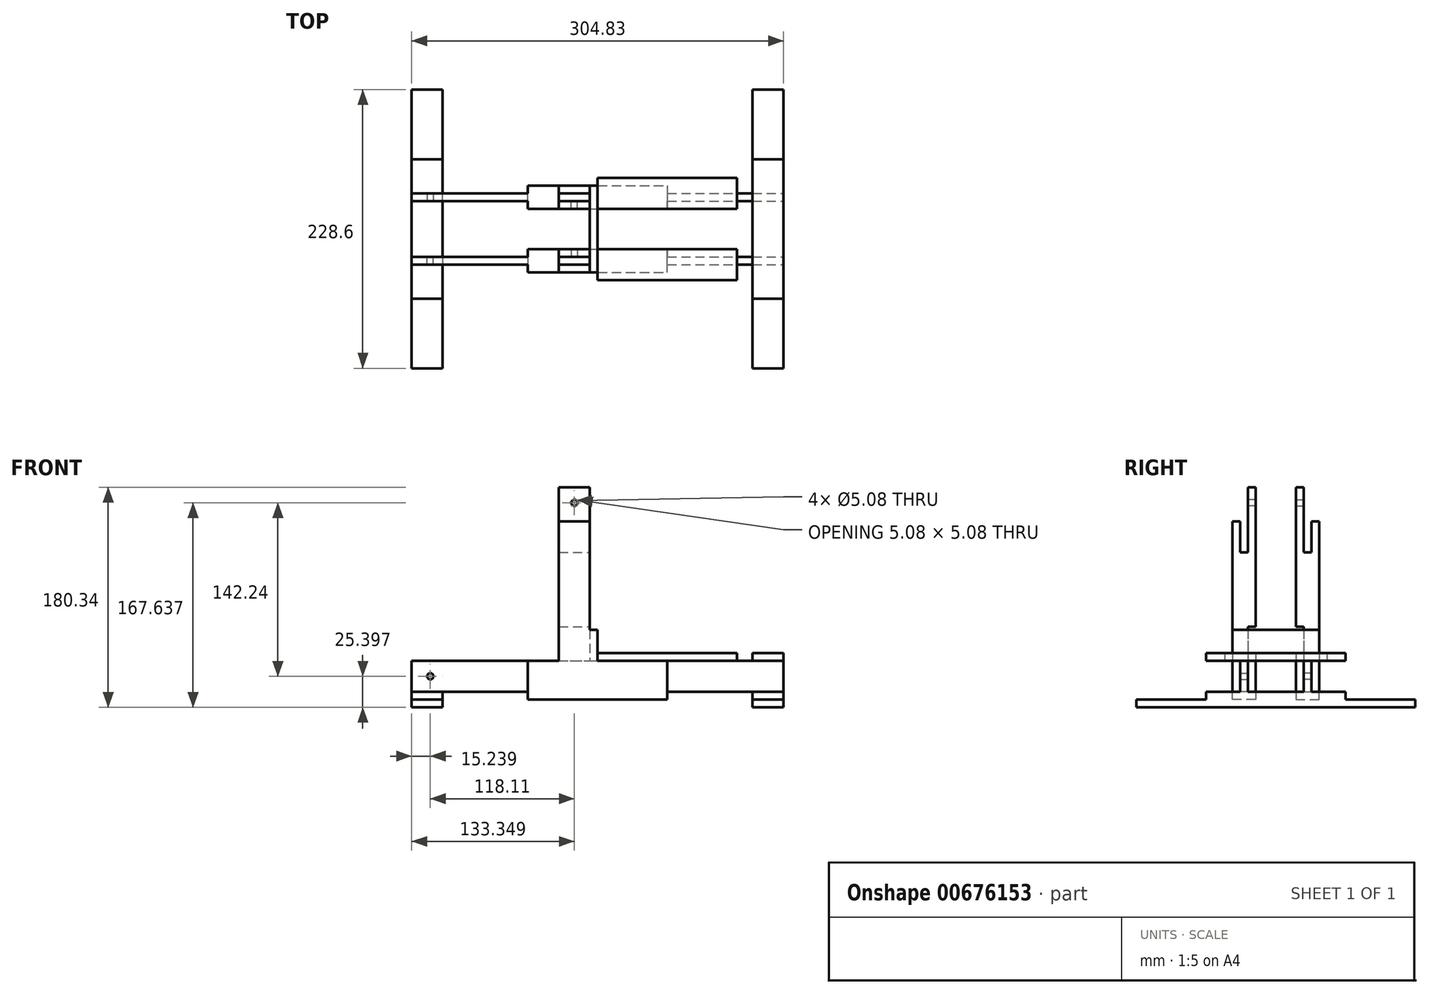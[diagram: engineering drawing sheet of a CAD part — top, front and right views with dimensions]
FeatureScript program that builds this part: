
annotation { "Feature Type Name" : "Feature", "Feature Type Description" : "" }
export const myFeature = defineFeature(function(context is Context, id is Id, definition is map)
    precondition{}
    {
        {
            var Q0;
            Q0=qCreatedBy(makeId("Front.planeOp"),FACE);
            var sketch = newSketch(context, id + "F0", { "sketchPlane" : qUnion([Q0])});
            skLineSegment(sketch, "E0.bottom", {"start": v(-142.94, -2.42) * mm, "end": v(161.86, -2.42) * mm});
            skLineSegment(sketch, "E0.top", {"start": v(-142.94, -27.82) * mm, "end": v(161.86, -27.82) * mm});
            skLineSegment(sketch, "E0.left", {"start": v(-142.94, -2.42) * mm, "end": v(-142.94, -27.82) * mm});
            skLineSegment(sketch, "E0.right", {"start": v(161.86, -2.42) * mm, "end": v(161.86, -27.82) * mm});
            skSolve(sketch);
        }
        {
            var Q0;
            Q0 = qSketchRegion(id + "F0", true);
            extrude(context, id + "F1", {"entities" : qUnion([Q0]), "depth" : 6.35 * mm, "offsetDistance" : 25.4 * mm});
        }
        {
            var Q0;
            Q0=makeQuery(id+"F1.opExtrude","CAP_FACE",FACE,{"disambiguationData":[OSD([sQuery(id+"F0.wireOp",EDGE,"E0.bottom"),sQuery(id+"F0.wireOp",EDGE,"E0.top"),sQuery(id+"F0.wireOp",EDGE,"E0.left"),sQuery(id+"F0.wireOp",EDGE,"E0.right")])],"isStart":false});
            var sketch = newSketch(context, id + "F2", { "sketchPlane" : qUnion([Q0])});
            skLineSegment(sketch, "E1.bottom", {"start": v(-47.7, -2.42) * mm, "end": v(66.6, -2.42) * mm});
            skLineSegment(sketch, "E1.top", {"start": v(-47.7, -27.82) * mm, "end": v(66.6, -27.82) * mm});
            skLineSegment(sketch, "E1.left", {"start": v(-47.7, -2.42) * mm, "end": v(-47.7, -27.82) * mm});
            skLineSegment(sketch, "E1.right", {"start": v(66.6, -2.42) * mm, "end": v(66.6, -27.82) * mm});
            skSolve(sketch);
        }
        {
            var Q0;
            Q0 = qSketchRegion(id + "F2", true);
            extrude(context, id + "F3", {"entities" : qUnion([Q0]), "operationType" : NewBodyOperationType.ADD, "depth" : 6.35 * mm, "offsetDistance" : 25.4 * mm});
        }
        {
            var Q0;
            Q0=makeQuery(id+"F1.opExtrude","CAP_FACE",FACE,{"disambiguationData":[OSD([sQuery(id+"F0.wireOp",EDGE,"E0.bottom"),sQuery(id+"F0.wireOp",EDGE,"E0.top"),sQuery(id+"F0.wireOp",EDGE,"E0.left"),sQuery(id+"F0.wireOp",EDGE,"E0.right")])],"isStart":true});
            var sketch = newSketch(context, id + "F4", { "sketchPlane" : qUnion([Q0])});
            skLineSegment(sketch, "E2.bottom", {"start": v(47.7, -27.82) * mm, "end": v(-66.6, -27.82) * mm});
            skLineSegment(sketch, "E2.top", {"start": v(47.7, -2.42) * mm, "end": v(-66.6, -2.42) * mm});
            skLineSegment(sketch, "E2.left", {"start": v(47.7, -27.82) * mm, "end": v(47.7, -2.42) * mm});
            skLineSegment(sketch, "E2.right", {"start": v(-66.6, -27.82) * mm, "end": v(-66.6, -2.42) * mm});
            skSolve(sketch);
        }
        {
            var Q0;
            Q0 = qSketchRegion(id + "F4", true);
            extrude(context, id + "F5", {"entities" : qUnion([Q0]), "operationType" : NewBodyOperationType.ADD, "depth" : 6.35 * mm, "offsetDistance" : 25.4 * mm});
        }
        {
            var Q0;
            {var subQ0=sQuery(id+"F0.wireOp",EDGE,"E0.left");var subQ1=sQuery(id+"F0.wireOp",EDGE,"E0.top");var subQ2=sQuery(id+"F0.wireOp",EDGE,"E0.bottom");Q0=makeQuery(id+"F3.boolean.opBoolean","SPLIT",FACE,{"disambiguationData":[TD([makeQuery(id+"F1.opExtrude","SWEPT_FACE",FACE,{"disambiguationData":[OSD([subQ0])]})])],"derivedFrom":makeQuery(id+"F1.opExtrude","CAP_FACE",FACE,{"disambiguationData":[OSD([subQ2,subQ1,subQ0,sQuery(id+"F0.wireOp",EDGE,"E0.right")])],"isStart":false})});}
            var sketch = newSketch(context, id + "F6", { "sketchPlane" : qUnion([Q0])});
            skCircle(sketch, "E3", {"center": v(-127.7, -15.12) * mm, "radius": 2.54 * mm});
            skPoint(sketch, "E3.centerSnap0", {"position": v(-142.94, -15.12) * mm});
            skSolve(sketch);
        }
        {
            var Q0;
            Q0=sQuery(id+"F6.wireOp",VERTEX,"E3.center");
            var Q1;
            Q1=makeQuery(id+"F1.opExtrude","SWEPT_BODY",BODY,{"disambiguationData":[OSD([sQuery(id+"F0.wireOp",EDGE,"E0.bottom"),sQuery(id+"F0.wireOp",EDGE,"E0.top"),sQuery(id+"F0.wireOp",EDGE,"E0.left"),sQuery(id+"F0.wireOp",EDGE,"E0.right")])]});
            hole(context, id + "F7", {"style" : HoleStyle.SIMPLE, "endStyle" : HoleEndStyle.THROUGH, "holeDiameter" : 5.08 * mm, "majorDiameter" : 6.35 * mm, "isTappedThrough" : true, "tappedDepth" : 12.7 * mm, "tapClearance" : 3, "locations" : qUnion([Q0]), "scope" : qUnion([Q1])});
        }
        {
            var Q0;
            Q0=makeQuery(id+"F5.boolean.opBoolean","MERGE",FACE,{"derivedFrom":[makeQuery(id+"F3.boolean.opBoolean","MERGE",FACE,{"derivedFrom":[makeQuery(id+"F1.opExtrude","SWEPT_FACE",FACE,{"disambiguationData":[OSD([sQuery(id+"F0.wireOp",EDGE,"E0.top")])]}),makeQuery(id+"F3.opExtrude","SWEPT_FACE",FACE,{"disambiguationData":[OSD([sQuery(id+"F2.wireOp",EDGE,"E1.top")])]})]}),makeQuery(id+"F5.opExtrude","SWEPT_FACE",FACE,{"disambiguationData":[OSD([sQuery(id+"F4.wireOp",EDGE,"E2.bottom")])]})]});
            var sketch = newSketch(context, id + "F8", { "sketchPlane" : qUnion([Q0])});
            skLineSegment(sketch, "E4.bottom", {"start": v(-47.7, 12.7) * mm, "end": v(66.6, 12.7) * mm});
            skLineSegment(sketch, "E4.top", {"start": v(-47.7, -6.35) * mm, "end": v(66.6, -6.35) * mm});
            skLineSegment(sketch, "E4.left", {"start": v(-47.7, 12.7) * mm, "end": v(-47.7, -6.35) * mm});
            skLineSegment(sketch, "E4.right", {"start": v(66.6, 12.7) * mm, "end": v(66.6, -6.35) * mm});
            skSolve(sketch);
        }
        {
            var Q0;
            Q0 = qSketchRegion(id + "F8", true);
            extrude(context, id + "F9", {"entities" : qUnion([Q0]), "operationType" : NewBodyOperationType.ADD, "depth" : 6.35 * mm, "offsetDistance" : 25.4 * mm});
        }
        {
            var Q0;
            {var subQ0=sQuery(id+"F0.wireOp",EDGE,"E0.left");var subQ2=sQuery(id+"F0.wireOp",EDGE,"E0.top");Q0=makeQuery(id+"F9.boolean.opBoolean","SPLIT",FACE,{"disambiguationData":[TD([makeQuery(id+"F1.opExtrude","SWEPT_FACE",FACE,{"disambiguationData":[OSD([subQ0])]})])],"derivedFrom":makeQuery(id+"F5.boolean.opBoolean","MERGE",FACE,{"derivedFrom":[makeQuery(id+"F3.boolean.opBoolean","MERGE",FACE,{"derivedFrom":[makeQuery(id+"F1.opExtrude","SWEPT_FACE",FACE,{"disambiguationData":[OSD([subQ2])]}),makeQuery(id+"F3.opExtrude","SWEPT_FACE",FACE,{"disambiguationData":[OSD([sQuery(id+"F2.wireOp",EDGE,"E1.top")])]})]}),makeQuery(id+"F5.opExtrude","SWEPT_FACE",FACE,{"disambiguationData":[OSD([sQuery(id+"F4.wireOp",EDGE,"E2.bottom")])]})]})});}
            var sketch = newSketch(context, id + "F10", { "sketchPlane" : qUnion([Q0])});
            skLineSegment(sketch, "E5.bottom", {"start": v(-142.94, 29.21) * mm, "end": v(-117.54, 29.21) * mm});
            skLineSegment(sketch, "E5.top", {"start": v(-142.94, -27.94) * mm, "end": v(-117.54, -27.94) * mm});
            skLineSegment(sketch, "E5.left", {"start": v(-142.94, 29.21) * mm, "end": v(-142.94, -27.94) * mm});
            skLineSegment(sketch, "E5.right", {"start": v(-117.54, 29.21) * mm, "end": v(-117.54, -27.94) * mm});
            skSolve(sketch);
        }
        {
            var Q0;
            Q0 = qSketchRegion(id + "F10", true);
            extrude(context, id + "F11", {"entities" : qUnion([Q0]), "operationType" : NewBodyOperationType.ADD, "depth" : 6.35 * mm, "offsetDistance" : 25.4 * mm});
        }
        {
            var Q0;
            Q0=makeQuery(id+"F11.opExtrude","CAP_FACE",FACE,{"disambiguationData":[OSD([sQuery(id+"F10.wireOp",EDGE,"E5.bottom"),sQuery(id+"F10.wireOp",EDGE,"E5.top"),sQuery(id+"F10.wireOp",EDGE,"E5.left"),sQuery(id+"F10.wireOp",EDGE,"E5.right")])],"isStart":false});
            var sketch = newSketch(context, id + "F12", { "sketchPlane" : qUnion([Q0])});
            skLineSegment(sketch, "E6.bottom", {"start": v(-142.94, 29.21) * mm, "end": v(-117.54, 29.21) * mm});
            skLineSegment(sketch, "E6.top", {"start": v(-142.94, -85.1) * mm, "end": v(-117.54, -85.1) * mm});
            skLineSegment(sketch, "E6.left", {"start": v(-142.94, 29.21) * mm, "end": v(-142.94, -85.1) * mm});
            skLineSegment(sketch, "E6.right", {"start": v(-117.54, 29.21) * mm, "end": v(-117.54, -85.1) * mm});
            skSolve(sketch);
        }
        {
            var Q0;
            Q0 = qSketchRegion(id + "F12", true);
            extrude(context, id + "F13", {"entities" : qUnion([Q0]), "operationType" : NewBodyOperationType.ADD, "depth" : 6.35 * mm, "offsetDistance" : 25.4 * mm});
        }
        {
            var Q0;
            {var subQ0=sQuery(id+"F0.wireOp",EDGE,"E0.right");var subQ2=sQuery(id+"F0.wireOp",EDGE,"E0.top");Q0=makeQuery(id+"F9.boolean.opBoolean","SPLIT",FACE,{"disambiguationData":[TD([makeQuery(id+"F1.opExtrude","SWEPT_FACE",FACE,{"disambiguationData":[OSD([subQ0])]})])],"derivedFrom":makeQuery(id+"F5.boolean.opBoolean","MERGE",FACE,{"derivedFrom":[makeQuery(id+"F3.boolean.opBoolean","MERGE",FACE,{"derivedFrom":[makeQuery(id+"F1.opExtrude","SWEPT_FACE",FACE,{"disambiguationData":[OSD([subQ2])]}),makeQuery(id+"F3.opExtrude","SWEPT_FACE",FACE,{"disambiguationData":[OSD([sQuery(id+"F2.wireOp",EDGE,"E1.top")])]})]}),makeQuery(id+"F5.opExtrude","SWEPT_FACE",FACE,{"disambiguationData":[OSD([sQuery(id+"F4.wireOp",EDGE,"E2.bottom")])]})]})});}
            var sketch = newSketch(context, id + "F14", { "sketchPlane" : qUnion([Q0])});
            skLineSegment(sketch, "E7.bottom", {"start": v(161.86, -27.94) * mm, "end": v(136.46, -27.94) * mm});
            skLineSegment(sketch, "E7.top", {"start": v(161.86, 29.2) * mm, "end": v(136.46, 29.2) * mm});
            skLineSegment(sketch, "E7.left", {"start": v(161.86, -27.94) * mm, "end": v(161.86, 29.2) * mm});
            skLineSegment(sketch, "E7.right", {"start": v(136.46, -27.94) * mm, "end": v(136.46, 29.2) * mm});
            skSolve(sketch);
        }
        {
            var Q0;
            Q0 = qSketchRegion(id + "F14", true);
            extrude(context, id + "F15", {"entities" : qUnion([Q0]), "operationType" : NewBodyOperationType.ADD, "depth" : 6.35 * mm, "offsetDistance" : 25.4 * mm});
        }
        {
            var Q0;
            Q0=makeQuery(id+"F15.opExtrude","CAP_FACE",FACE,{"disambiguationData":[OSD([sQuery(id+"F14.wireOp",EDGE,"E7.bottom"),sQuery(id+"F14.wireOp",EDGE,"E7.top"),sQuery(id+"F14.wireOp",EDGE,"E7.left"),sQuery(id+"F14.wireOp",EDGE,"E7.right")])],"isStart":false});
            var sketch = newSketch(context, id + "F16", { "sketchPlane" : qUnion([Q0])});
            skLineSegment(sketch, "E8.bottom", {"start": v(136.46, 29.2) * mm, "end": v(161.86, 29.2) * mm});
            skLineSegment(sketch, "E8.top", {"start": v(136.46, -85.1) * mm, "end": v(161.86, -85.1) * mm});
            skLineSegment(sketch, "E8.left", {"start": v(136.46, 29.2) * mm, "end": v(136.46, -85.1) * mm});
            skLineSegment(sketch, "E8.right", {"start": v(161.86, 29.21) * mm, "end": v(161.86, -85.1) * mm});
            skSolve(sketch);
        }
        {
            var Q0;
            Q0 = qSketchRegion(id + "F16", true);
            extrude(context, id + "F17", {"entities" : qUnion([Q0]), "operationType" : NewBodyOperationType.ADD, "depth" : 6.35 * mm, "offsetDistance" : 25.4 * mm});
        }
        {
            var Q0;
            Q0=makeQuery(id+"F5.boolean.opBoolean","MERGE",FACE,{"derivedFrom":[makeQuery(id+"F3.boolean.opBoolean","MERGE",FACE,{"derivedFrom":[makeQuery(id+"F1.opExtrude","SWEPT_FACE",FACE,{"disambiguationData":[OSD([sQuery(id+"F0.wireOp",EDGE,"E0.bottom")])]}),makeQuery(id+"F3.opExtrude","SWEPT_FACE",FACE,{"disambiguationData":[OSD([sQuery(id+"F2.wireOp",EDGE,"E1.bottom")])]})]}),makeQuery(id+"F5.opExtrude","SWEPT_FACE",FACE,{"disambiguationData":[OSD([sQuery(id+"F4.wireOp",EDGE,"E2.top")])]})]});
            var sketch = newSketch(context, id + "F18", { "sketchPlane" : qUnion([Q0])});
            skLineSegment(sketch, "E9.bottom", {"start": v(161.9, -29.21) * mm, "end": v(136.5, -29.21) * mm});
            skLineSegment(sketch, "E9.top", {"start": v(161.9, 27.94) * mm, "end": v(136.5, 27.94) * mm});
            skLineSegment(sketch, "E9.left", {"start": v(161.9, -29.21) * mm, "end": v(161.9, 27.94) * mm});
            skLineSegment(sketch, "E9.right", {"start": v(136.5, -29.21) * mm, "end": v(136.5, 27.94) * mm});
            skSolve(sketch);
        }
        {
            var Q0;
            Q0 = qSketchRegion(id + "F18", true);
            extrude(context, id + "F19", {"entities" : qUnion([Q0]), "operationType" : NewBodyOperationType.ADD, "depth" : 6.35 * mm, "offsetDistance" : 25.4 * mm});
        }
        {
            var Q0;
            Q0=makeQuery(id+"F5.boolean.opBoolean","MERGE",FACE,{"derivedFrom":[makeQuery(id+"F3.boolean.opBoolean","MERGE",FACE,{"derivedFrom":[makeQuery(id+"F1.opExtrude","SWEPT_FACE",FACE,{"disambiguationData":[OSD([sQuery(id+"F0.wireOp",EDGE,"E0.bottom")])]}),makeQuery(id+"F3.opExtrude","SWEPT_FACE",FACE,{"disambiguationData":[OSD([sQuery(id+"F2.wireOp",EDGE,"E1.bottom")])]})]}),makeQuery(id+"F5.opExtrude","SWEPT_FACE",FACE,{"disambiguationData":[OSD([sQuery(id+"F4.wireOp",EDGE,"E2.top")])]})]});
            var sketch = newSketch(context, id + "F20", { "sketchPlane" : qUnion([Q0])});
            skLineSegment(sketch, "E10.bottom", {"start": v(9.46, -50.8) * mm, "end": v(3.1, -50.8) * mm});
            skLineSegment(sketch, "E10.top", {"start": v(9.46, 6.35) * mm, "end": v(3.1, 6.35) * mm});
            skLineSegment(sketch, "E10.left", {"start": v(9.46, -50.8) * mm, "end": v(9.46, 6.35) * mm});
            skLineSegment(sketch, "E10.right", {"start": v(3.1, -50.8) * mm, "end": v(3.1, 6.35) * mm});
            skSolve(sketch);
        }
        {
            var Q0;
            Q0 = qSketchRegion(id + "F20", true);
            extrude(context, id + "F21", {"entities" : qUnion([Q0]), "operationType" : NewBodyOperationType.ADD, "depth" : 25.4 * mm, "offsetDistance" : 25.4 * mm});
        }
        {
            var Q0;
            {var subQ1=sQuery(id+"F2.wireOp",EDGE,"E1.right");var subQ2=sQuery(id+"F2.wireOp",EDGE,"E1.bottom");var subQ4=sQuery(id+"F4.wireOp",EDGE,"E2.top");var subQ8=sQuery(id+"F0.wireOp",EDGE,"E0.bottom");Q0=makeQuery(id+"F21.boolean.opBoolean","SPLIT",FACE,{"disambiguationData":[TD([makeQuery(id+"F3.opExtrude","SWEPT_FACE",FACE,{"disambiguationData":[OSD([subQ1])]})])],"derivedFrom":makeQuery(id+"F5.boolean.opBoolean","MERGE",FACE,{"derivedFrom":[makeQuery(id+"F3.boolean.opBoolean","MERGE",FACE,{"derivedFrom":[makeQuery(id+"F1.opExtrude","SWEPT_FACE",FACE,{"disambiguationData":[OSD([subQ8])]}),makeQuery(id+"F3.opExtrude","SWEPT_FACE",FACE,{"disambiguationData":[OSD([subQ2])]})]}),makeQuery(id+"F5.opExtrude","SWEPT_FACE",FACE,{"disambiguationData":[OSD([subQ4])]})]})});}
            var sketch = newSketch(context, id + "F22", { "sketchPlane" : qUnion([Q0])});
            skLineSegment(sketch, "E11.bottom", {"start": v(9.46, -12.7) * mm, "end": v(123.76, -12.7) * mm});
            skLineSegment(sketch, "E11.top", {"start": v(9.46, 12.7) * mm, "end": v(123.76, 12.7) * mm});
            skLineSegment(sketch, "E11.left", {"start": v(9.46, -12.7) * mm, "end": v(9.46, 12.7) * mm});
            skLineSegment(sketch, "E11.right", {"start": v(123.76, -12.7) * mm, "end": v(123.76, 12.7) * mm});
            skSolve(sketch);
        }
        {
            var Q0;
            Q0 = qSketchRegion(id + "F22", true);
            extrude(context, id + "F23", {"entities" : qUnion([Q0]), "operationType" : NewBodyOperationType.ADD, "depth" : 6.35 * mm, "offsetDistance" : 25.4 * mm});
        }
        {
            var Q0;
            {var subQ0=sQuery(id+"F0.wireOp",EDGE,"E0.left");var subQ3=sQuery(id+"F0.wireOp",EDGE,"E0.bottom");var subQ5=sQuery(id+"F4.wireOp",EDGE,"E2.top");var subQ7=sQuery(id+"F2.wireOp",EDGE,"E1.bottom");Q0=makeQuery(id+"F21.boolean.opBoolean","SPLIT",FACE,{"disambiguationData":[TD([makeQuery(id+"F1.opExtrude","SWEPT_FACE",FACE,{"disambiguationData":[OSD([subQ0])]})])],"derivedFrom":makeQuery(id+"F5.boolean.opBoolean","MERGE",FACE,{"derivedFrom":[makeQuery(id+"F3.boolean.opBoolean","MERGE",FACE,{"derivedFrom":[makeQuery(id+"F1.opExtrude","SWEPT_FACE",FACE,{"disambiguationData":[OSD([subQ3])]}),makeQuery(id+"F3.opExtrude","SWEPT_FACE",FACE,{"disambiguationData":[OSD([subQ7])]})]}),makeQuery(id+"F5.opExtrude","SWEPT_FACE",FACE,{"disambiguationData":[OSD([subQ5])]})]})});}
            var sketch = newSketch(context, id + "F24", { "sketchPlane" : qUnion([Q0])});
            skLineSegment(sketch, "E12.bottom", {"start": v(-22.3, 0) * mm, "end": v(3.1, 0) * mm});
            skLineSegment(sketch, "E12.top", {"start": v(-22.3, -6.35) * mm, "end": v(3.1, -6.35) * mm});
            skLineSegment(sketch, "E12.left", {"start": v(-22.3, 0) * mm, "end": v(-22.3, -6.35) * mm});
            skLineSegment(sketch, "E12.right", {"start": v(3.1, 0) * mm, "end": v(3.1, -6.35) * mm});
            skSolve(sketch);
        }
        {
            var Q0;
            Q0 = qSketchRegion(id + "F24", true);
            extrude(context, id + "F25", {"entities" : qUnion([Q0]), "operationType" : NewBodyOperationType.ADD, "depth" : 88.9 * mm, "offsetDistance" : 25.4 * mm});
        }
        {
            var Q0;
            {var subQ0=sQuery(id+"F0.wireOp",EDGE,"E0.left");var subQ3=sQuery(id+"F0.wireOp",EDGE,"E0.bottom");var subQ5=sQuery(id+"F4.wireOp",EDGE,"E2.top");var subQ7=sQuery(id+"F2.wireOp",EDGE,"E1.bottom");Q0=makeQuery(id+"F21.boolean.opBoolean","SPLIT",FACE,{"disambiguationData":[TD([makeQuery(id+"F1.opExtrude","SWEPT_FACE",FACE,{"disambiguationData":[OSD([subQ0])]})])],"derivedFrom":makeQuery(id+"F5.boolean.opBoolean","MERGE",FACE,{"derivedFrom":[makeQuery(id+"F3.boolean.opBoolean","MERGE",FACE,{"derivedFrom":[makeQuery(id+"F1.opExtrude","SWEPT_FACE",FACE,{"disambiguationData":[OSD([subQ3])]}),makeQuery(id+"F3.opExtrude","SWEPT_FACE",FACE,{"disambiguationData":[OSD([subQ7])]})]}),makeQuery(id+"F5.opExtrude","SWEPT_FACE",FACE,{"disambiguationData":[OSD([subQ5])]})]})});}
            var sketch = newSketch(context, id + "F26", { "sketchPlane" : qUnion([Q0])});
            skLineSegment(sketch, "E13.bottom", {"start": v(-22.3, 6.35) * mm, "end": v(3.1, 6.35) * mm});
            skLineSegment(sketch, "E13.top", {"start": v(-22.3, 0) * mm, "end": v(3.1, 0) * mm});
            skLineSegment(sketch, "E13.left", {"start": v(-22.3, 6.35) * mm, "end": v(-22.3, 0) * mm});
            skLineSegment(sketch, "E13.right", {"start": v(3.1, 6.35) * mm, "end": v(3.1, 0) * mm});
            skSolve(sketch);
        }
        {
            var Q0;
            Q0 = qSketchRegion(id + "F26", true);
            extrude(context, id + "F27", {"entities" : qUnion([Q0]), "operationType" : NewBodyOperationType.ADD, "depth" : 114.3 * mm, "offsetDistance" : 25.4 * mm});
        }
        {
            var Q0;
            Q0=makeQuery(id+"F25.opExtrude","SWEPT_FACE",FACE,{"disambiguationData":[OSD([sQuery(id+"F24.wireOp",EDGE,"E12.top")])]});
            var sketch = newSketch(context, id + "F28", { "sketchPlane" : qUnion([Q0])});
            skLineSegment(sketch, "E14.bottom", {"start": v(-22.3, 25.52) * mm, "end": v(3.1, 25.52) * mm});
            skLineSegment(sketch, "E14.top", {"start": v(-22.3, 139.82) * mm, "end": v(3.1, 139.82) * mm});
            skLineSegment(sketch, "E14.left", {"start": v(-22.3, 25.52) * mm, "end": v(-22.3, 139.82) * mm});
            skLineSegment(sketch, "E14.right", {"start": v(3.1, 25.52) * mm, "end": v(3.1, 139.82) * mm});
            skSolve(sketch);
        }
        {
            var Q0;
            Q0 = qSketchRegion(id + "F28", true);
            extrude(context, id + "F29", {"entities" : qUnion([Q0]), "operationType" : NewBodyOperationType.ADD, "depth" : 6.35 * mm, "offsetDistance" : 25.4 * mm});
        }
        {
            var Q0;
            Q0=makeQuery(id+"F29.opExtrude","CAP_FACE",FACE,{"disambiguationData":[OSD([sQuery(id+"F28.wireOp",EDGE,"E14.bottom"),sQuery(id+"F28.wireOp",EDGE,"E14.top"),sQuery(id+"F28.wireOp",EDGE,"E14.left"),sQuery(id+"F28.wireOp",EDGE,"E14.right")])],"isStart":true});
            var sketch = newSketch(context, id + "F30", { "sketchPlane" : qUnion([Q0])});
            skCircle(sketch, "E15", {"center": v(9.6, 127.12) * mm, "radius": 2.54 * mm});
            skPoint(sketch, "E15.centerSnap0", {"position": v(9.6, 139.82) * mm});
            skSolve(sketch);
        }
        {
            var Q0;
            Q0=sQuery(id+"F30.wireOp",VERTEX,"E15.center");
            var Q1;
            Q1=makeQuery(id+"F1.opExtrude","SWEPT_BODY",BODY,{"disambiguationData":[OSD([sQuery(id+"F0.wireOp",EDGE,"E0.bottom"),sQuery(id+"F0.wireOp",EDGE,"E0.top"),sQuery(id+"F0.wireOp",EDGE,"E0.left"),sQuery(id+"F0.wireOp",EDGE,"E0.right")])]});
            hole(context, id + "F31", {"style" : HoleStyle.SIMPLE, "endStyle" : HoleEndStyle.THROUGH, "holeDiameter" : 5.08 * mm, "majorDiameter" : 6.35 * mm, "isTappedThrough" : true, "tappedDepth" : 12.7 * mm, "tapClearance" : 3, "locations" : qUnion([Q0]), "scope" : qUnion([Q1])});
        }
        {
            var Q0;
            Q0=makeQuery(id+"F1.opExtrude","SWEPT_BODY",BODY,{"disambiguationData":[OSD([sQuery(id+"F0.wireOp",EDGE,"E0.bottom"),sQuery(id+"F0.wireOp",EDGE,"E0.top"),sQuery(id+"F0.wireOp",EDGE,"E0.left"),sQuery(id+"F0.wireOp",EDGE,"E0.right")])]});
            var Q1;
            Q1=makeQuery(id+"F13.boolean.opBoolean","MERGE",FACE,{"derivedFrom":[makeQuery(id+"F11.opExtrude","SWEPT_FACE",FACE,{"disambiguationData":[OSD([sQuery(id+"F10.wireOp",EDGE,"E5.bottom")])]}),makeQuery(id+"F13.opExtrude","SWEPT_FACE",FACE,{"disambiguationData":[OSD([sQuery(id+"F12.wireOp",EDGE,"E6.bottom")])]})]});
            mirror(context, id + "F32", {"operationType" : NewBodyOperationType.ADD, "entities" : qUnion([Q0]), "mirrorPlane" : qUnion([Q1])});
        }
    });
